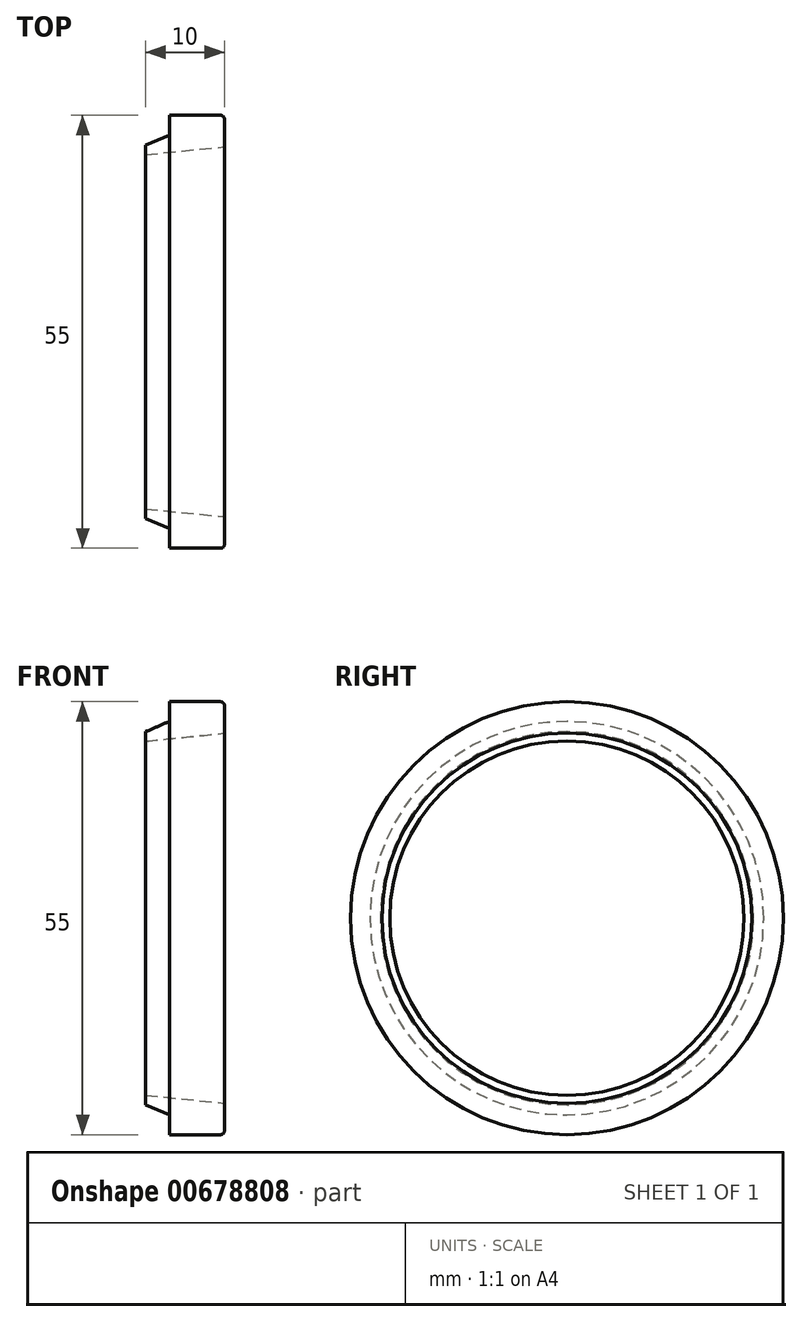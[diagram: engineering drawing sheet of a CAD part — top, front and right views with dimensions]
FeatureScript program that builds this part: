
annotation { "Feature Type Name" : "Feature", "Feature Type Description" : "" }
export const myFeature = defineFeature(function(context is Context, id is Id, definition is map)
    precondition{}
    {
        {
            var Q0;
            Q0=qCreatedBy(makeId("Front.planeOp"),FACE);
            var sketch = newSketch(context, id + "F0", { "sketchPlane" : qUnion([Q0])});
            skLineSegment(sketch, "E0", {"start": v(0, 22.5) * mm, "end": v(10, 23.5) * mm});
            skLineSegment(sketch, "E1", {"start": v(10, 23.5) * mm, "end": v(10, 27.5) * mm});
            skLineSegment(sketch, "E2", {"start": v(10, 27.5) * mm, "end": v(3, 27.5) * mm});
            skLineSegment(sketch, "E3", {"start": v(3, 27.5) * mm, "end": v(3, 25) * mm});
            skLineSegment(sketch, "E4", {"start": v(3, 25) * mm, "end": v(0, 23.7) * mm});
            skLineSegment(sketch, "E5", {"start": v(0, 23.7) * mm, "end": v(0, 22.5) * mm});
            skSolve(sketch);
        }
        {
            var Q0;
            Q0=qCreatedBy(makeId("Front.planeOp"),FACE);
            var sketch = newSketch(context, id + "F1", { "sketchPlane" : qUnion([Q0])});
            skLineSegment(sketch, "E6", {"start": v(-22.66, 0) * mm, "end": v(26.8, 0) * mm});
            skSolve(sketch);
        }
        {
            var Q0;
            Q0 = qSketchRegion(id + "F0", true);
            var Q1;
            Q1=sQuery(id+"F1.wireOp",EDGE,"E6");
            revolve(context, id + "F2", {"entities" : qUnion([Q0]), "axis" : qUnion([Q1]), "revolveType" : RevolveType.FULL});
        }
        {
            var Q0;
            Q0=makeQuery(id+"F2.opRevolve","SWEPT_EDGE",EDGE,{"disambiguationData":[OSD([sQuery(id+"F0.wireOp",EDGE,"E1"),sQuery(id+"F0.wireOp",EDGE,"E2")])]});
            fillet(context, id + "F3", {"entities" : qUnion([Q0]), "radius" : 0.5 * mm, "tangentPropagation" : true, "allowEdgeOverflow" : false});
        }
    });
